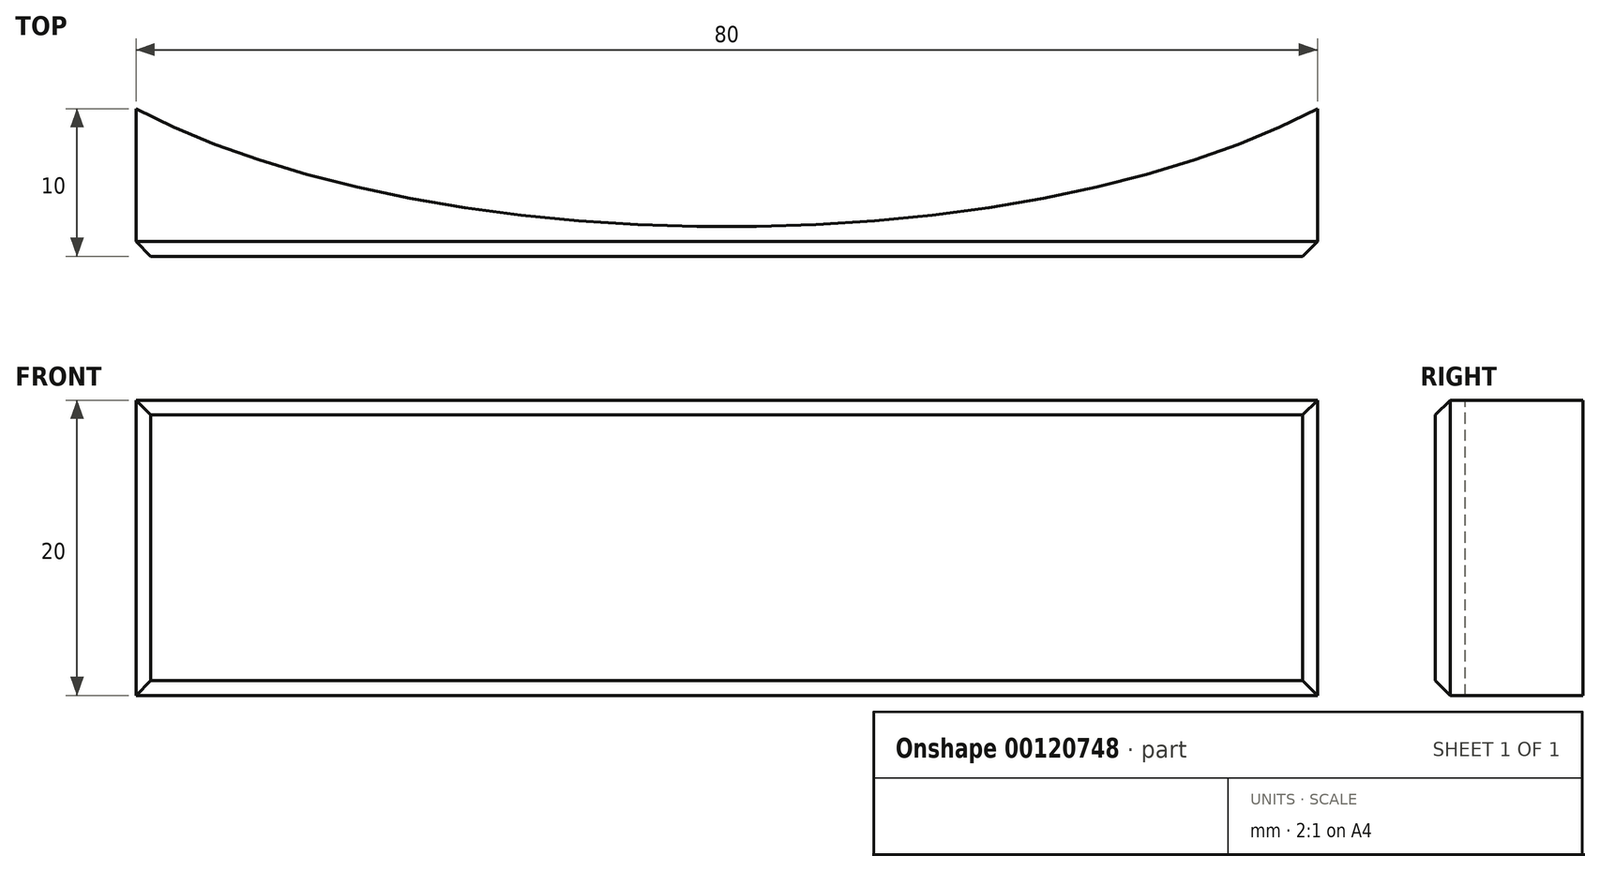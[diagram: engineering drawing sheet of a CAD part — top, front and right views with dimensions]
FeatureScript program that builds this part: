
annotation { "Feature Type Name" : "Feature", "Feature Type Description" : "" }
export const myFeature = defineFeature(function(context is Context, id is Id, definition is map)
    precondition{}
    {
        {
            var Q0;
            Q0=qCreatedBy(makeId("Top.planeOp"),FACE);
            var sketch = newSketch(context, id + "F0", { "sketchPlane" : qUnion([Q0])});
            skLineSegment(sketch, "E0", {"start": v(0, 20) * mm, "end": v(0, 0) * mm, "construction": true});
            skLineSegment(sketch, "E1", {"start": v(0, 0) * mm, "end": v(50, 0) * mm, "construction": true});
            skEllipticalArc(sketch, "E2", {});
            skPoint(sketch, "E3", {"position": v(-50, 0) * mm});
            skLineSegment(sketch, "E4", {"start": v(-40, -12) * mm, "end": v(-40, -22) * mm});
            skLineSegment(sketch, "E5.MirrorCS", {"start": v(40, -12) * mm, "end": v(40, -22) * mm});
            skLineSegment(sketch, "E6", {"start": v(-40, -22) * mm, "end": v(40, -22) * mm});
            skPoint(sketch, "E7", {"position": v(0, -20) * mm});
            const initialGuessF0  = {"E2": [0, 0, 1, 0, 0.05, 0.02, 3.7850937623830774, 5.639684198386302]};
            skSetInitialGuess(sketch, initialGuessF0);
            skSolve(sketch);
        }
        {
            var Q0;
            Q0 = qSketchRegion(id + "F0", true);
            extrude(context, id + "F1", {"entities" : qUnion([Q0]), "depth" : 20 * mm});
        }
        {
            var Q0;
            Q0=makeQuery(id+"F1.opExtrude","SWEPT_EDGE",EDGE,{"disambiguationData":[OSD([sQuery(id+"F0.wireOp",EDGE,"E4"),sQuery(id+"F0.wireOp",EDGE,"E6")])]});
            var Q1;
            Q1=makeQuery(id+"F1.opExtrude","CAP_EDGE",EDGE,{"disambiguationData":[OSD([sQuery(id+"F0.wireOp",EDGE,"E6")])],"isStart":false});
            var Q2;
            Q2=makeQuery(id+"F1.opExtrude","CAP_EDGE",EDGE,{"disambiguationData":[OSD([sQuery(id+"F0.wireOp",EDGE,"E6")])],"isStart":true});
            var Q3;
            Q3=makeQuery(id+"F1.opExtrude","SWEPT_EDGE",EDGE,{"disambiguationData":[OSD([sQuery(id+"F0.wireOp",EDGE,"E5.MirrorCS"),sQuery(id+"F0.wireOp",EDGE,"E6")])]});
            chamfer(context, id + "F2", {"entities" : qUnion([Q0, Q1, Q2, Q3]), "width" : 1 * mm, "tangentPropagation" : true});
        }
    });
